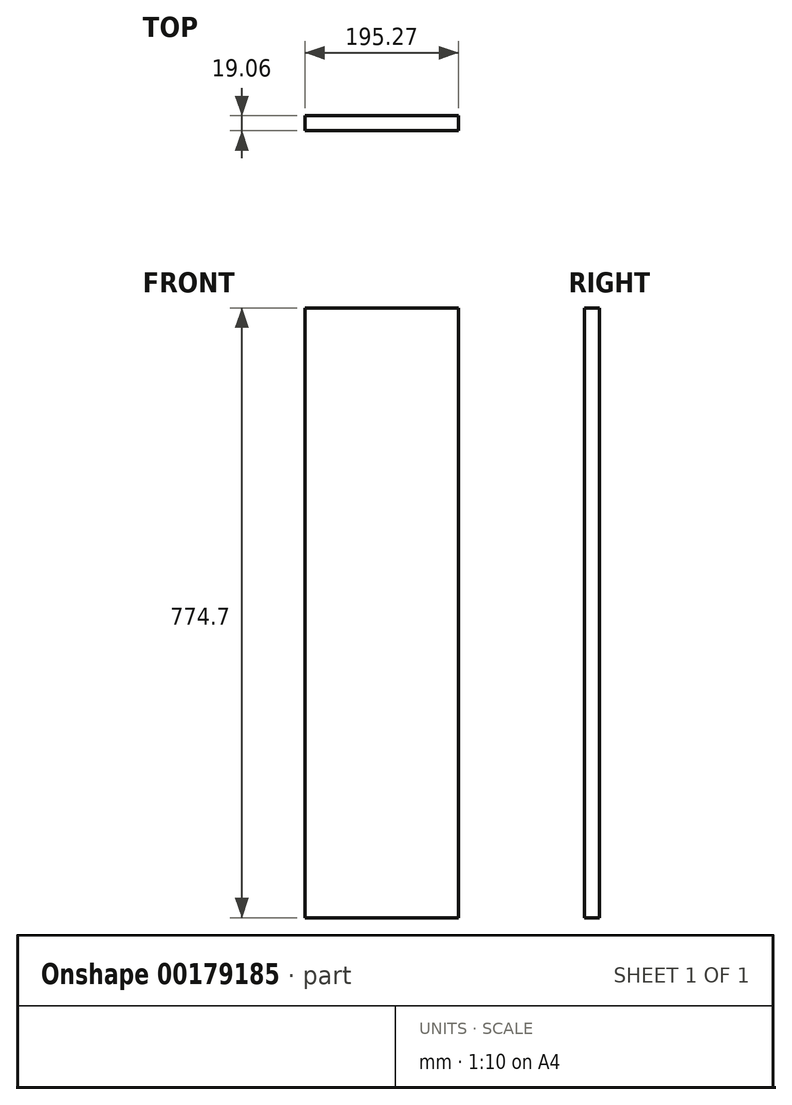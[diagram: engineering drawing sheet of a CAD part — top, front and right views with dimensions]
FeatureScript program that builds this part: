
annotation { "Feature Type Name" : "Feature", "Feature Type Description" : "" }
export const myFeature = defineFeature(function(context is Context, id is Id, definition is map)
    precondition{}
    {
        {
            var Q0;
            Q0=qCreatedBy(makeId("Front.planeOp"),FACE);
            var sketch = newSketch(context, id + "F0", { "sketchPlane" : qUnion([Q0])});
            skLineSegment(sketch, "E0.bottom", {"start": v(-189.17, 387.35) * mm, "end": v(6.1, 387.35) * mm});
            skLineSegment(sketch, "E0.top", {"start": v(-189.17, -387.35) * mm, "end": v(6.1, -387.35) * mm});
            skLineSegment(sketch, "E0.left", {"start": v(-189.17, 387.35) * mm, "end": v(-189.17, -387.35) * mm});
            skLineSegment(sketch, "E0.right", {"start": v(6.1, 387.35) * mm, "end": v(6.1, -387.35) * mm});
            skLineSegment(sketch, "E1", {"start": v(-189.17, 0) * mm, "end": v(6.1, 0) * mm});
            skSolve(sketch);
        }
        {
            var Q0;
            {var subQ0=sQuery(id+"F0.wireOp",EDGE,"E0.bottom");Q0=makeQuery(id+"F0.imprint","IMPRINT",FACE,{"disambiguationData":[TD([[makeQuery(id+"F0.imprint","IMPRINT",EDGE,{"derivedFrom":subQ0}),-1.0]])]});}
            var Q1;
            {var subQ0=sQuery(id+"F0.wireOp",EDGE,"E0.top");Q1=makeQuery(id+"F0.imprint","IMPRINT",FACE,{"disambiguationData":[TD([[makeQuery(id+"F0.imprint","IMPRINT",EDGE,{"derivedFrom":subQ0}),1.0]])]});}
            extrude(context, id + "F1", {"entities" : qUnion([Q0, Q1]), "depth" : 19.05 * mm, "symmetric" : true});
        }
    });
